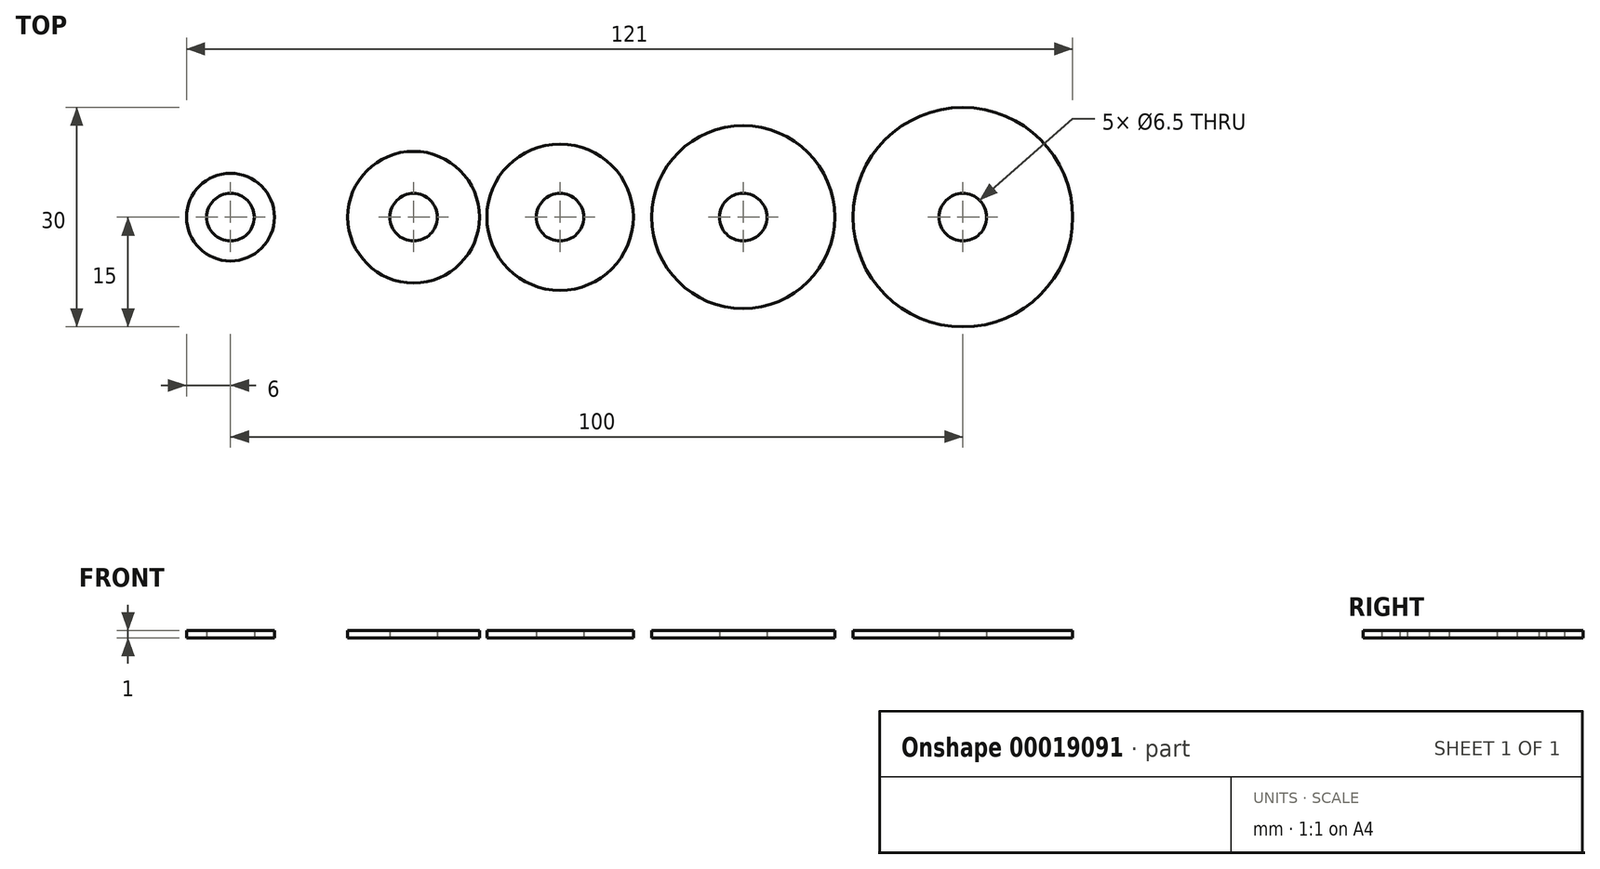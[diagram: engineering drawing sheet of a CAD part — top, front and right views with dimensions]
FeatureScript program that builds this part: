
annotation { "Feature Type Name" : "Feature", "Feature Type Description" : "" }
export const myFeature = defineFeature(function(context is Context, id is Id, definition is map)
    precondition{}
    {
        {
            var Q0;
            Q0=qCreatedBy(makeId("Top.planeOp"),FACE);
            var sketch = newSketch(context, id + "F0", { "sketchPlane" : qUnion([Q0])});
            skLineSegment(sketch, "E0", {"start": v(-33.08, 0) * mm, "end": v(99.25, 0) * mm, "construction": true});
            skCircle(sketch, "E1", {"center": v(-15, 0) * mm, "radius": 3.25 * mm});
            skCircle(sketch, "E2", {"center": v(-15, 0) * mm, "radius": 6 * mm});
            skCircle(sketch, "E3", {"center": v(10, 0) * mm, "radius": 3.25 * mm});
            skCircle(sketch, "E4", {"center": v(10, 0) * mm, "radius": 9 * mm});
            skCircle(sketch, "E5", {"center": v(30, 0) * mm, "radius": 3.25 * mm});
            skCircle(sketch, "E6", {"center": v(30, 0) * mm, "radius": 10 * mm});
            skCircle(sketch, "E7", {"center": v(55, 0) * mm, "radius": 3.25 * mm});
            skCircle(sketch, "E8", {"center": v(55, 0) * mm, "radius": 12.5 * mm});
            skCircle(sketch, "E9", {"center": v(85, 0) * mm, "radius": 3.25 * mm});
            skCircle(sketch, "E10", {"center": v(85, 0) * mm, "radius": 15 * mm});
            skPoint(sketch, "E11", {"position": v(0, 0) * mm});
            skSolve(sketch);
        }
        {
            var Q0;
            Q0=qSketchRegion(id+"F0",true);
            extrude(context, id + "F1", {"entities" : qUnion([Q0]), "depth" : 1 * mm});
        }
    });
